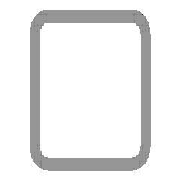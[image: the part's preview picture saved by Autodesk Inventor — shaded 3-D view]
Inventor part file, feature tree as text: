
AUTODESK INVENTOR PART (.ipt)
format: ipt  version: 2025.1 (Build 291241020, 241B)  size: 132,608 bytes
history: native  units: mm (DEFAULTED — no unit token found)
features: other x4, sketch x1, plane x1
ambient origin geometry x8: Origin, YZ Plane, XZ Plane, XY Plane, X Axis, Y Axis, Z Axis, Center Point
bodies: Solid1 (feature_tree), Body (feature_tree)
feature tree (6):
  parser-record x1  (decoder bookkeeping rows leaked as tree rows — omitted from the tree; the rows remain in map.json)
  other  "Driven Length"
  other  "Start Plane"
  other  "End Plane"
  sketch  "Sketch3"  dims[d3=1300.0mm d4=0.0mm d7=6.0mm d9=100.0mm d11=100.0mm d12=3.0mm d13=-0.0mm d14=1300.0mm d15=50.0mm d16=50.0mm d17=90.0deg d18=1300.0mm]
  plane  "Work Plane3"
